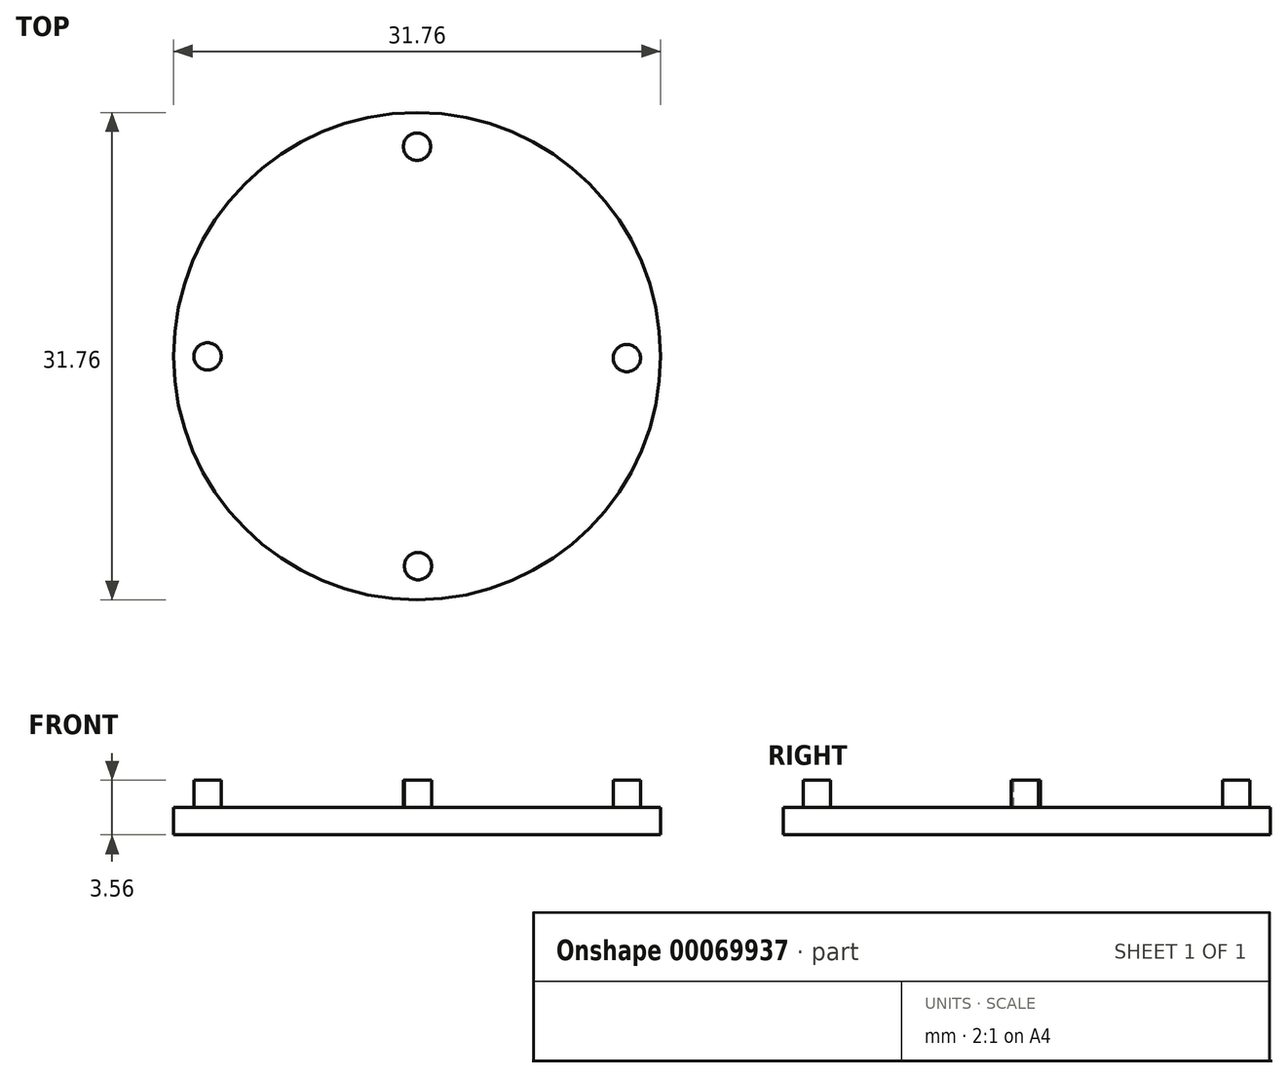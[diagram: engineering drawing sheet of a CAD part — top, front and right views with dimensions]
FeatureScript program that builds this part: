
annotation { "Feature Type Name" : "Feature", "Feature Type Description" : "" }
export const myFeature = defineFeature(function(context is Context, id is Id, definition is map)
    precondition{}
    {
        {
            var Q0;
            Q0=qCreatedBy(makeId("Top.planeOp"),FACE);
            var sketch = newSketch(context, id + "F0", { "sketchPlane" : qUnion([Q0])});
            skCircle(sketch, "E0", {"center": v(0, 0) * mm, "radius": 15.88 * mm});
            skSolve(sketch);
        }
        {
            var Q0;
            Q0 = qSketchRegion(id + "F0", true);
            extrude(context, id + "F1", {"entities" : qUnion([Q0]), "oppositeDirection" : true, "depth" : 1.78 * mm});
        }
        {
            var Q0;
            Q0=makeQuery(id+"F1.opExtrude","CAP_FACE",FACE,{"disambiguationData":[OSD([sQuery(id+"F0.wireOp",EDGE,"E0")])],"isStart":true});
            var sketch = newSketch(context, id + "F2", { "sketchPlane" : qUnion([Q0])});
            skCircle(sketch, "E1", {"center": v(0, 0) * mm, "radius": 12.7 * mm});
            skSolve(sketch);
        }
        {
            var Q0;
            Q0=makeQuery(id+"F2.imprint","IMPRINT",FACE,{"disambiguationData":[TD([[makeQuery(id+"F2.imprint","IMPRINT",EDGE,{"derivedFrom":sQuery(id+"F2.wireOp",EDGE,"E1")}),-1.0]])]});
            var sketch = newSketch(context, id + "F3", { "sketchPlane" : qUnion([Q0])});
            skCircle(sketch, "E2", {"center": v(0, 13.65) * mm, "radius": 0.89 * mm});
            skCircle(sketch, "E3", {"center": v(-13.66, -0.02) * mm, "radius": 0.89 * mm});
            skCircle(sketch, "E4", {"center": v(0.06, -13.68) * mm, "radius": 0.89 * mm});
            skCircle(sketch, "E5", {"center": v(13.67, -0.12) * mm, "radius": 0.89 * mm});
            skSolve(sketch);
        }
        {
            var Q0;
            Q0 = qSketchRegion(id + "F3", true);
            extrude(context, id + "F4", {"entities" : qUnion([Q0]), "operationType" : NewBodyOperationType.ADD, "depth" : 1.78 * mm});
        }
    });
